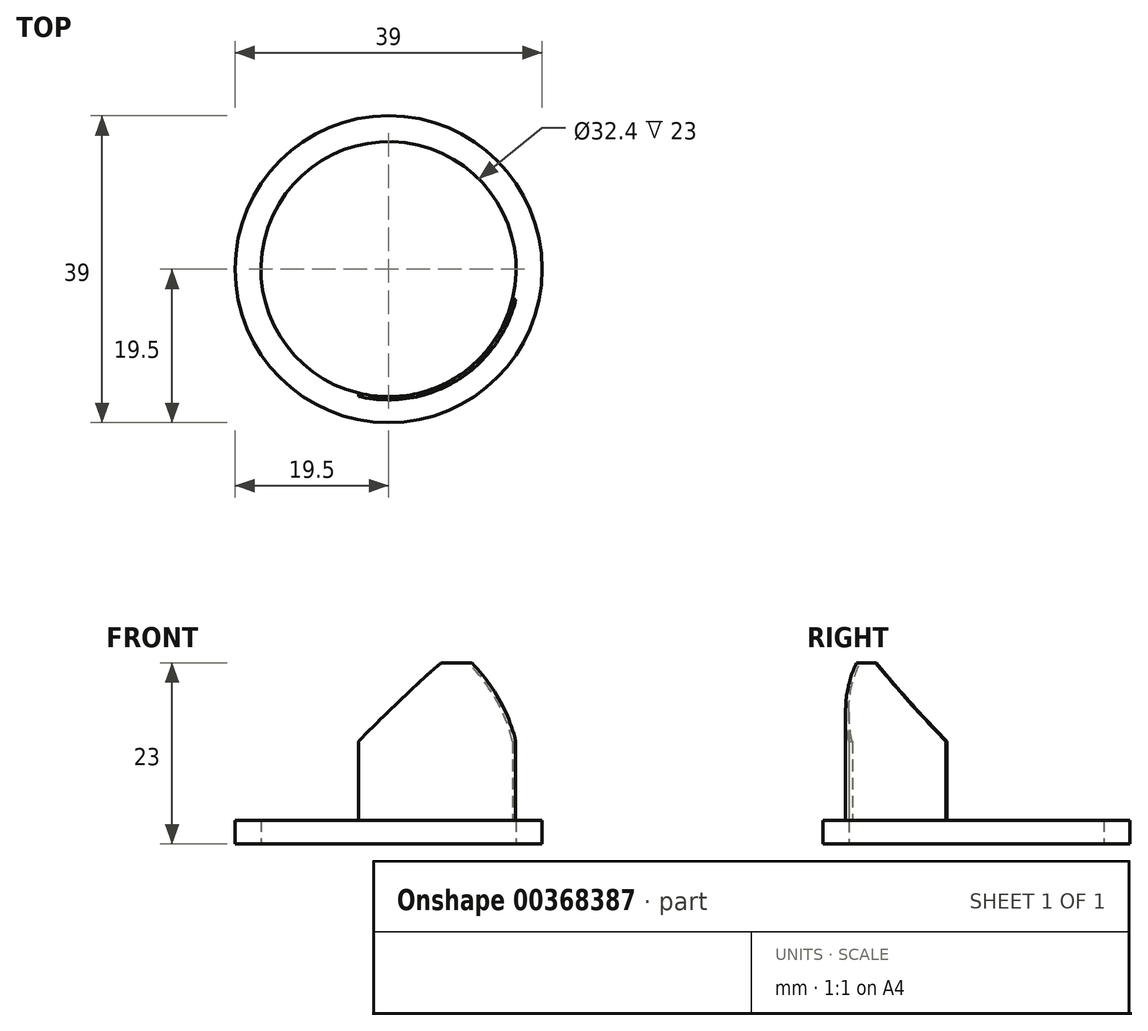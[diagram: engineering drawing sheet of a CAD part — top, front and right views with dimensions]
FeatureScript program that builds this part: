
annotation { "Feature Type Name" : "Feature", "Feature Type Description" : "" }
export const myFeature = defineFeature(function(context is Context, id is Id, definition is map)
    precondition{}
    {
        {
            var Q0;
            Q0=qCreatedBy(makeId("Top.planeOp"),FACE);
            var sketch = newSketch(context, id + "F0", { "sketchPlane" : qUnion([Q0])});
            skCircle(sketch, "E0", {"center": v(0, 0) * mm, "radius": 16.2 * mm});
            skCircle(sketch, "E1", {"center": v(0, 0) * mm, "radius": 16.6 * mm});
            skLineSegment(sketch, "E2", {"start": v(0, 0) * mm, "end": v(16.15, -3.83) * mm});
            skLineSegment(sketch, "E3", {"start": v(0, 0) * mm, "end": v(-3.83, -16.15) * mm});
            skSolve(sketch);
        }
        {
            var Q0;
            {var subQ0=sQuery(id+"F0.wireOp",EDGE,"E2");var subQ1=sQuery(id+"F0.wireOp",EDGE,"E0");var subQ2=makeQuery(id+"F0.imprint","INTERSECT",VERTEX,{"derivedFrom":[subQ1,subQ0]});Q0=makeQuery(id+"F0.imprint","IMPRINT",FACE,{"disambiguationData":[TD([[makeQuery(id+"F0.imprint","IMPRINT",EDGE,{"disambiguationData":[TD([[subQ2,1.0]])],"derivedFrom":subQ1}),-1.0]])]});}
            extrude(context, id + "F1", {"entities" : qUnion([Q0]), "depth" : 20 * mm});
        }
        {
            var Q0;
            Q0=qCreatedBy(makeId("Top.planeOp"),FACE);
            var sketch = newSketch(context, id + "F2", { "sketchPlane" : qUnion([Q0])});
            skCircle(sketch, "E4", {"center": v(0, 0) * mm, "radius": 16.2 * mm});
            skCircle(sketch, "E5", {"center": v(0, 0) * mm, "radius": 19.5 * mm});
            skSolve(sketch);
        }
        {
            var Q0;
            Q0 = qSketchRegion(id + "F2", true);
            extrude(context, id + "F3", {"entities" : qUnion([Q0]), "operationType" : NewBodyOperationType.ADD, "oppositeDirection" : true, "depth" : 3 * mm});
        }
        {
            var Q0;
            Q0=makeQuery(id+"F1.opExtrude","CAP_EDGE",EDGE,{"disambiguationData":[OSD([sQuery(id+"F0.wireOp",EDGE,"E2")])],"isStart":false});
            var Q1;
            Q1=makeQuery(id+"F1.opExtrude","CAP_EDGE",EDGE,{"disambiguationData":[OSD([sQuery(id+"F0.wireOp",EDGE,"E3")])],"isStart":false});
            chamfer(context, id + "F4", {"entities" : qUnion([Q0, Q1]), "width" : 10 * mm, "tangentPropagation" : true});
        }
    });
